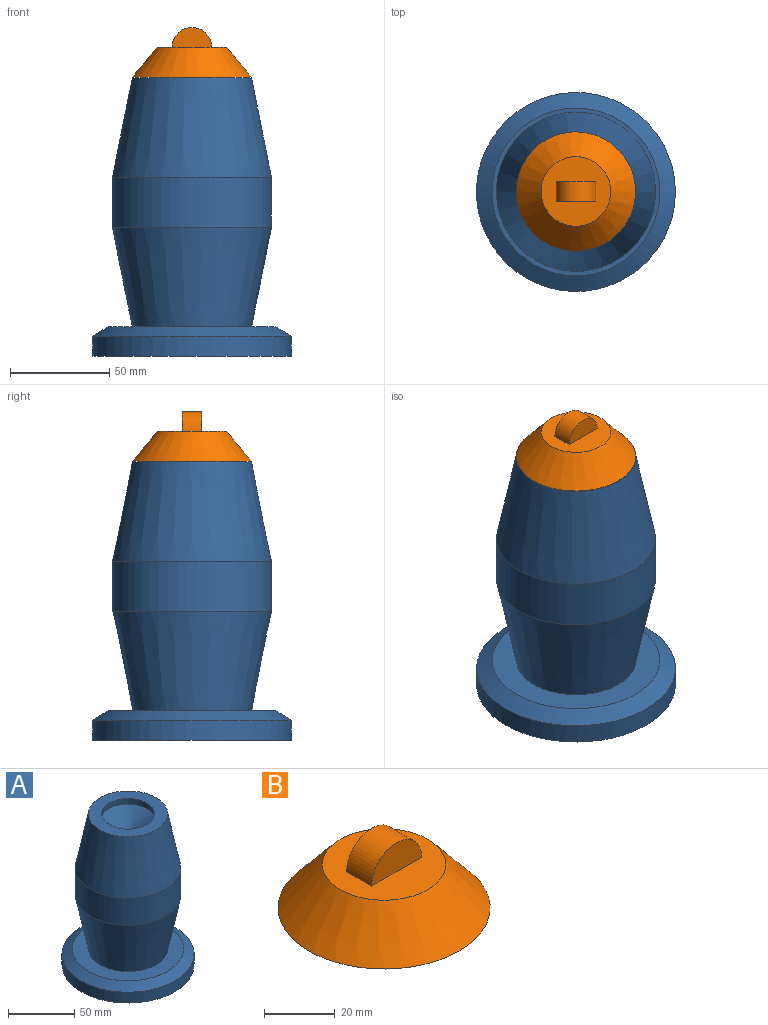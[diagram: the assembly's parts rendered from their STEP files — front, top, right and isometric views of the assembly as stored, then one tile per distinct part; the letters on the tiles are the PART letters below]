
ASSEMBLY  parts=2 mates=1
PART A: 10 faces, bbox 100x100x140 mm
  f0: cylinder r=50mm len=100mm, axis (0,0,-1), area 3141.6mm2, adj f1,f3
  f1: plane 100x100mm, normal (0,0,-1), area 7854mm2, adj f0
  f2: plane 84.34x84.34mm, normal (0,0,1), area 2759.3mm2, adj f3,f4
  f3: cone r=50mm half-angle=57.4deg, axis (0,0,-1), area 2690.1mm2, adj f0,f2
  f4: cone r=30mm half-angle=11.3deg, axis (0,0,1), area 11213.3mm2, adj f2,f5
  f5: cylinder r=40mm len=80mm, axis (0,0,-1), area 6283.2mm2, adj f4,f6
  f6: cone r=40mm half-angle=11.3deg, axis (0,0,-1), area 11213.3mm2, adj f5,f7
  f7: plane 60x60mm, normal (0,0,1), area 1570.8mm2, adj f6,f9
  f8: cone r=0mm half-angle=59deg, axis (0,0,1), area 1466mm2, adj f9
  f9: cylinder r=20mm len=40mm, axis (0,0,1), area 628.3mm2, adj f7,f8
PART B: 8 faces, bbox 60x60x30 mm
  f0: cylinder r=20mm len=40mm, axis (0,0,-1), area 628.3mm2, adj f1,f2
  f1: plane 40x40mm, normal (0,0,-1), area 1256.6mm2, adj f0
  f2: plane 60x60mm, normal (0,0,-1), area 1570.8mm2, adj f0,f4
  f3: plane 35x35mm, normal (0,0,1), area 762.1mm2, adj f4,f5,f6,f7
  f4: cone r=30mm half-angle=39.8deg, axis (0,0,-1), area 2913.7mm2, adj f2,f3
  f5: cylinder r=10mm len=20mm, axis (0,1,0), area 314.2mm2, adj f3,f6,f7
  f6: plane 20x10mm, normal (0,-1,0), area 157.1mm2, adj f3,f5
  f7: plane 20x10mm, normal (0,1,0), area 157.1mm2, adj f3,f5
PLACE A t=(0.32,0.09,-127.79)mm
PLACE B t=(0.32,0.09,2.57)mm
MATE slider B.f0 <-> A.f8  axis (0,0,-1) through (0.32,0.09,2.57)mm
